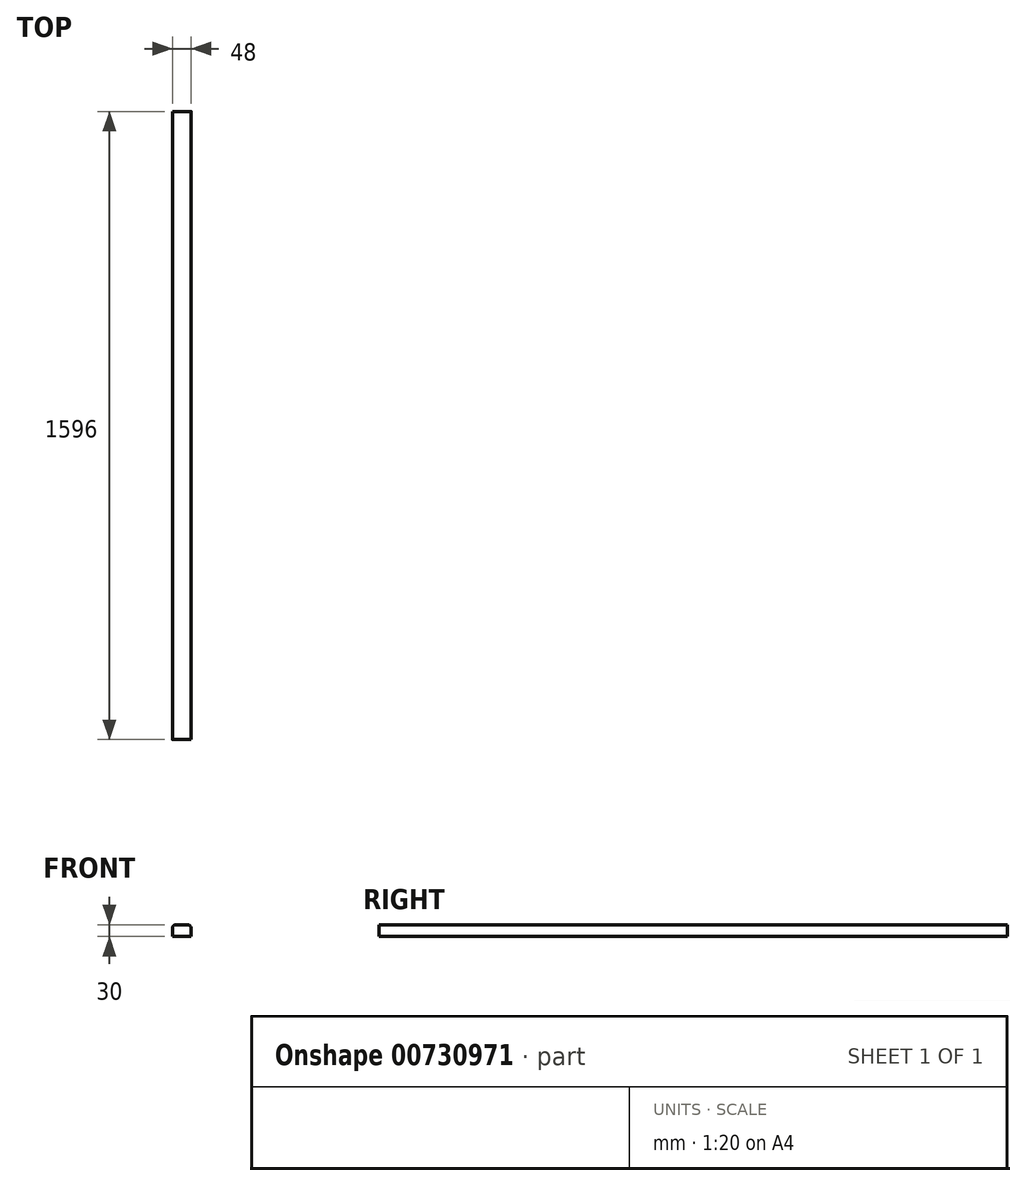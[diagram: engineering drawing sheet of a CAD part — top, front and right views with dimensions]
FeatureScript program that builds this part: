
annotation { "Feature Type Name" : "Feature", "Feature Type Description" : "" }
export const myFeature = defineFeature(function(context is Context, id is Id, definition is map)
    precondition{}
    {
        {
            var Q0;
            Q0=qCreatedBy(makeId("Front.planeOp"),FACE);
            var sketch = newSketch(context, id + "F0", { "sketchPlane" : qUnion([Q0])});
            skLineSegment(sketch, "E0.bottom", {"start": v(24, -15) * mm, "end": v(-24, -15) * mm});
            skLineSegment(sketch, "E0.top", {"start": v(24, 15) * mm, "end": v(-24, 15) * mm});
            skLineSegment(sketch, "E0.left", {"start": v(24, -15) * mm, "end": v(24, 15) * mm});
            skLineSegment(sketch, "E0.right", {"start": v(-24, -15) * mm, "end": v(-24, 15) * mm});
            skPoint(sketch, "E0.middle", {"position": v(0, 0) * mm});
            skSolve(sketch);
        }
        {
            var Q0;
            Q0=makeQuery(id+"F0.imprint","IMPRINT",FACE,{"disambiguationData":[TD([[makeQuery(id+"F0.imprint","IMPRINT",EDGE,{"derivedFrom":sQuery(id+"F0.wireOp",EDGE,"E0.bottom")}),-1.0]])]});
            extrude(context, id + "F1", {"entities" : qUnion([Q0]), "depth" : 1596 * mm, "offsetDistance" : 25 * mm});
        }
        {
            var Q0;
            Q0=makeQuery(id+"F1.opExtrude","SWEPT_EDGE",EDGE,{"disambiguationData":[OSD([sQuery(id+"F0.wireOp",EDGE,"E0.top"),sQuery(id+"F0.wireOp",EDGE,"E0.right")])]});
            var Q1;
            Q1=makeQuery(id+"F1.opExtrude","SWEPT_EDGE",EDGE,{"disambiguationData":[OSD([sQuery(id+"F0.wireOp",EDGE,"E0.top"),sQuery(id+"F0.wireOp",EDGE,"E0.left")])]});
            fillet(context, id + "F2", {"entities" : qUnion([Q0, Q1]), "radius" : 10 * mm, "tangentPropagation" : true, "allowEdgeOverflow" : false});
        }
    });
